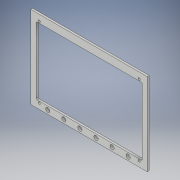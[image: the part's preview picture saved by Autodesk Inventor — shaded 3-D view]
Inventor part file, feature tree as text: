
AUTODESK INVENTOR PART (.ipt)
format: ipt  version: 2019 (Build 230136000, 136)  size: 137,728 bytes
history: native  units: in
note: dims shown in document units (in); Inventor stores cm internally (conversion verified against a paired STEP export)
features: reference x18, plane x2, other x2, sketch x1, extrude x1
ambient origin geometry x8: Origin, YZ Plane, XZ Plane, XY Plane, X Axis, Y Axis, Z Axis, Center Point
bodies: Body1 (feature_tree)
feature tree (24):
  plane  "Work Plane1"
  sketch  "Sketch1"  dims[d1=5.125in d2=7.25in d3=0.5in d4=0.2677in d5=2.3622in d7=1.0in d8=0.3937in d10=1.0in d18=0.05in d19=0.125in d20=0.0in]
  plane  "Work Plane2"
  extrude  "Extrusion2"  Depth=7.25in
  reference  "Reference1"
  reference  "Reference2"
  reference  "Reference3"
  reference  "Reference4"
  reference  "Reference5"
  reference  "Reference6"
  reference  "Reference7"
  reference  "Reference8"
  reference  "Reference9"
  reference  "Reference10"
  reference  "Reference11"
  reference  "Reference12"
  reference  "Reference13"
  reference  "Reference14"
  reference  "Reference15"
  reference  "Reference16"
  reference  "Reference17"
  reference  "Reference18"
  other  "Assembly1"
  other  "NHD-7:1"
